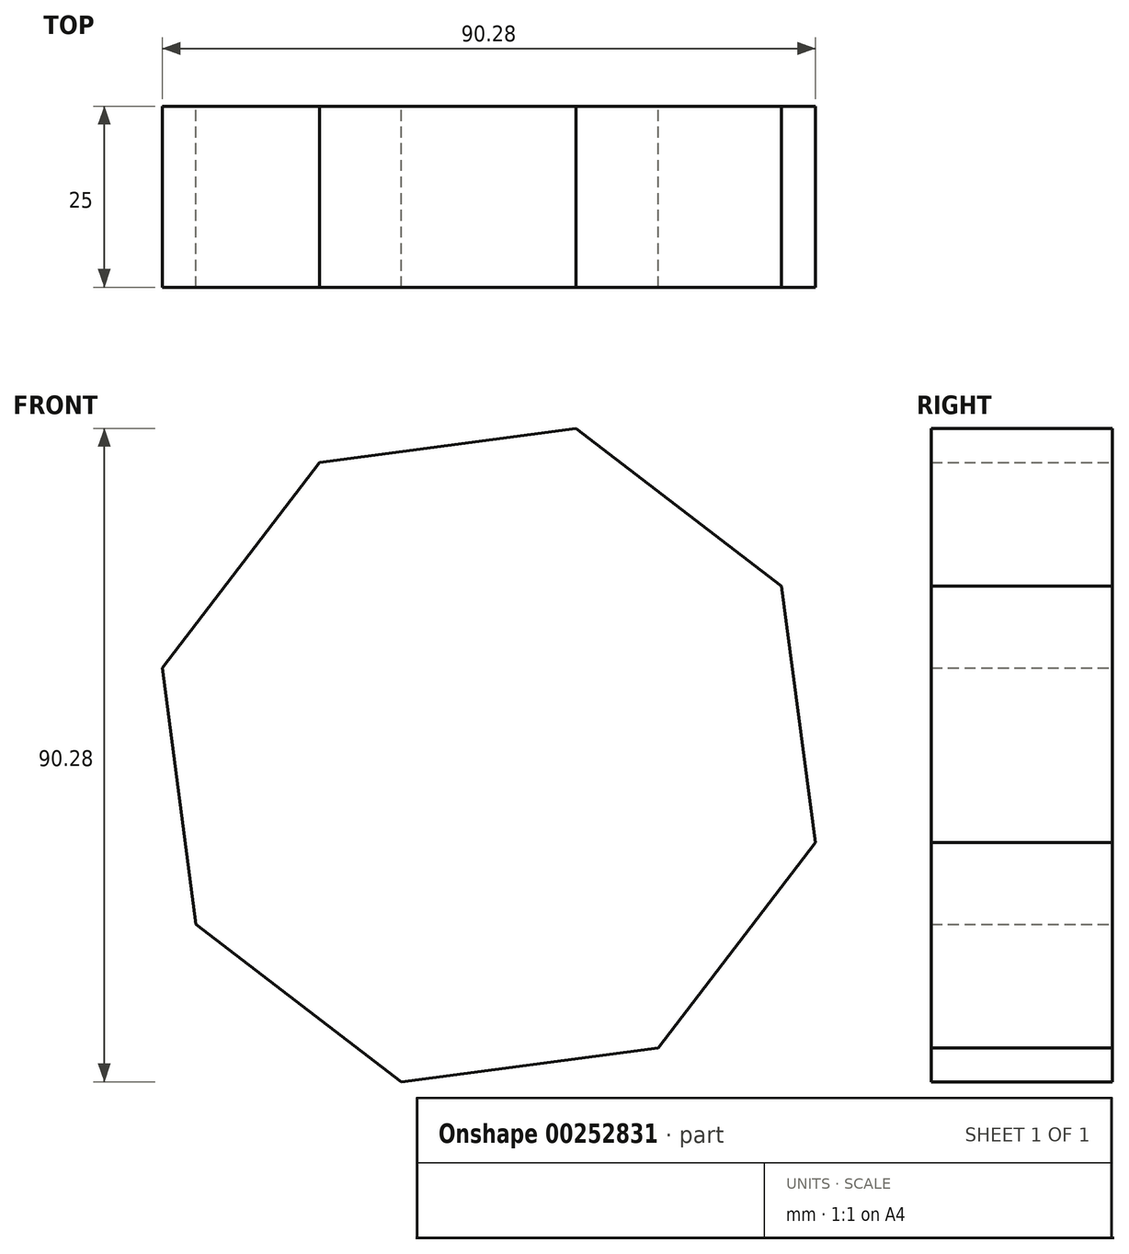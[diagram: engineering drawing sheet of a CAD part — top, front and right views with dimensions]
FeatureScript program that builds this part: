
annotation { "Feature Type Name" : "Feature", "Feature Type Description" : "" }
export const myFeature = defineFeature(function(context is Context, id is Id, definition is map)
    precondition{}
    {
        {
            var Q0;
            Q0=qCreatedBy(makeId("Front.planeOp"),FACE);
            var sketch = newSketch(context, id + "F0", { "sketchPlane" : qUnion([Q0])});
            skCircle(sketch, "E0.cCircle", {"center": v(0, 0) * mm, "radius": 46.72 * mm, "construction": true});
            skLineSegment(sketch, "E0.0", {"start": v(40.45, 23.38) * mm, "end": v(45.14, -12.07) * mm});
            skLineSegment(sketch, "E0.1", {"start": v(45.14, -12.07) * mm, "end": v(23.38, -40.45) * mm});
            skLineSegment(sketch, "E0.2", {"start": v(23.38, -40.45) * mm, "end": v(-12.07, -45.14) * mm});
            skLineSegment(sketch, "E0.3", {"start": v(-12.07, -45.14) * mm, "end": v(-40.45, -23.38) * mm});
            skLineSegment(sketch, "E0.4", {"start": v(-40.45, -23.38) * mm, "end": v(-45.14, 12.07) * mm});
            skLineSegment(sketch, "E0.5", {"start": v(-45.14, 12.07) * mm, "end": v(-23.38, 40.45) * mm});
            skLineSegment(sketch, "E0.6", {"start": v(-23.38, 40.45) * mm, "end": v(12.07, 45.14) * mm});
            skLineSegment(sketch, "E0.7", {"start": v(12.07, 45.14) * mm, "end": v(40.45, 23.38) * mm});
            skSolve(sketch);
        }
        {
            var Q0;
            Q0=makeQuery(id+"F0.imprint","IMPRINT",FACE,{"disambiguationData":[TD([[makeQuery(id+"F0.imprint","IMPRINT",EDGE,{"derivedFrom":sQuery(id+"F0.wireOp",EDGE,"E0.0")}),-1.0]])]});
            extrude(context, id + "F1", {"entities" : qUnion([Q0]), "endBound" : BoundingType.SYMMETRIC, "depth" : 25 * mm});
        }
    });
